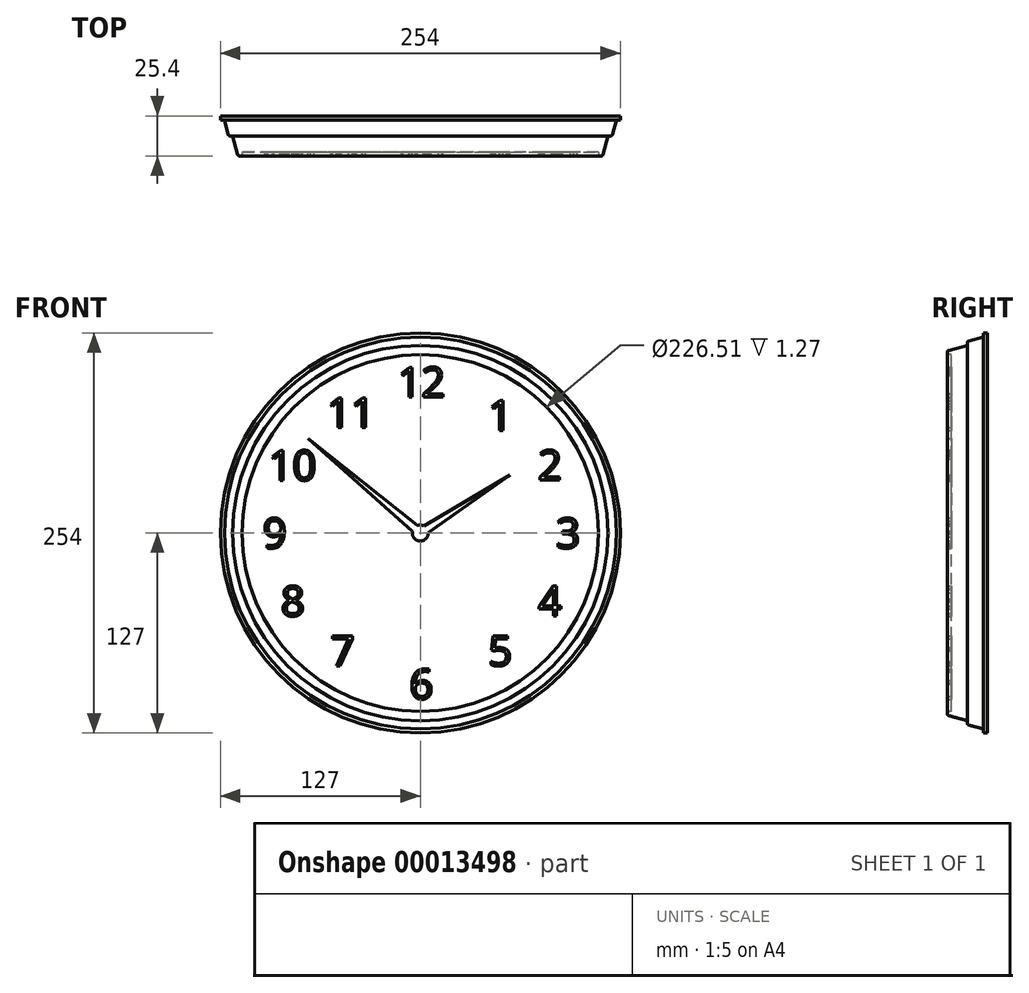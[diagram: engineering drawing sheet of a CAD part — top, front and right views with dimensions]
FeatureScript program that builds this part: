
annotation { "Feature Type Name" : "Feature", "Feature Type Description" : "" }
export const myFeature = defineFeature(function(context is Context, id is Id, definition is map)
    precondition{}
    {
        {
            var Q0;
            Q0=qCreatedBy(makeId("Right.planeOp"),FACE);
            var sketch = newSketch(context, id + "F0", { "sketchPlane" : qUnion([Q0])});
            skLineSegment(sketch, "E0", {"start": v(0, 0) * mm, "end": v(0, 127) * mm});
            skLineSegment(sketch, "E1", {"start": v(0, 127) * mm, "end": v(-2.54, 127) * mm});
            skLineSegment(sketch, "E2", {"start": v(-2.54, 127) * mm, "end": v(-2.54, 124.46) * mm});
            skLineSegment(sketch, "E3", {"start": v(-2.54, 124.46) * mm, "end": v(-11.76, 121.99) * mm});
            skLineSegment(sketch, "E4", {"start": v(-12.7, 120.76) * mm, "end": v(-12.7, 119.2) * mm});
            skLineSegment(sketch, "E5", {"start": v(-12.7, 119.2) * mm, "end": v(-24.46, 116.05) * mm});
            skLineSegment(sketch, "E6", {"start": v(-25.4, 114.82) * mm, "end": v(-25.4, 114.52) * mm});
            skLineSegment(sketch, "E7", {"start": v(-24.13, 113.25) * mm, "end": v(-22.86, 113.25) * mm});
            skLineSegment(sketch, "E8", {"start": v(-22.86, 113.25) * mm, "end": v(-22.86, 0) * mm});
            skLineSegment(sketch, "E9", {"start": v(-22.86, 0) * mm, "end": v(0, 0) * mm});
            skPoint(sketch, "E10.visualSharp", {"position": v(-12.7, 121.74) * mm});
            skArc(sketch, "E10.filletArc", {"start": v(-11.76, 121.99) * mm, "mid": v(-12.44, 121.54) * mm, "end": v(-12.7, 120.76) * mm});
            skPoint(sketch, "E11.visualSharp", {"position": v(-25.4, 115.8) * mm});
            skArc(sketch, "E11.filletArc", {"start": v(-24.46, 116.05) * mm, "mid": v(-25.14, 115.6) * mm, "end": v(-25.4, 114.82) * mm});
            skPoint(sketch, "E12.visualSharp", {"position": v(-25.4, 113.25) * mm});
            skArc(sketch, "E12.filletArc", {"start": v(-25.4, 114.52) * mm, "mid": v(-25.03, 113.63) * mm, "end": v(-24.13, 113.25) * mm});
            skSolve(sketch);
        }
        {
            var Q0;
            Q0 = qSketchRegion(id + "F0", true);
            var Q1;
            Q1=sQuery(id+"F0.wireOp",EDGE,"E9");
            revolve(context, id + "F1", {"entities" : qUnion([Q0]), "axis" : qUnion([Q1]), "revolveType" : RevolveType.FULL});
        }
        {
            var Q0;
            Q0=makeQuery(id+"F1.opRevolve","SWEPT_FACE",FACE,{"disambiguationData":[OSD([sQuery(id+"F0.wireOp",EDGE,"E8")])]});
            var sketch = newSketch(context, id + "F2", { "sketchPlane" : qUnion([Q0])});
            skText(sketch, "E13", { "text": "12", "fontName": "OpenSans-Regular.ttf"});
            skLineSegment(sketch, "E14", {"start": v(43.18, 74.79) * mm, "end": v(0, 0) * mm, "construction": true});
            skLineSegment(sketch, "E15", {"start": v(0, 0) * mm, "end": v(74.79, 43.18) * mm, "construction": true});
            skLineSegment(sketch, "E16", {"start": v(0, 0) * mm, "end": v(86.36, 0) * mm, "construction": true});
            skLineSegment(sketch, "E17", {"start": v(74.79, -43.18) * mm, "end": v(0, 0) * mm, "construction": true});
            skLineSegment(sketch, "E18", {"start": v(0, 0) * mm, "end": v(43.18, -74.79) * mm, "construction": true});
            skLineSegment(sketch, "E19", {"start": v(0, 0) * mm, "end": v(0, 86.36) * mm, "construction": true});
            skText(sketch, "E20", { "text": "1", "fontName": "OpenSans-Regular.ttf"});
            skText(sketch, "E21", { "text": "2", "fontName": "OpenSans-Regular.ttf"});
            skText(sketch, "E22", { "text": "3", "fontName": "OpenSans-Regular.ttf"});
            skLineSegment(sketch, "E23", {"start": v(0, 0) * mm, "end": v(0, -86.36) * mm, "construction": true});
            skText(sketch, "E24", { "text": "4", "fontName": "OpenSans-Regular.ttf"});
            skText(sketch, "E25", { "text": "5", "fontName": "OpenSans-Regular.ttf"});
            skText(sketch, "E26", { "text": "6", "fontName": "OpenSans-Regular.ttf"});
            skLineSegment(sketch, "E27", {"start": v(0, 0) * mm, "end": v(-43.18, -74.79) * mm, "construction": true});
            skLineSegment(sketch, "E28", {"start": v(0, 0) * mm, "end": v(-74.79, -43.18) * mm, "construction": true});
            skLineSegment(sketch, "E29", {"start": v(0, 0) * mm, "end": v(-74.79, 43.18) * mm, "construction": true});
            skLineSegment(sketch, "E30", {"start": v(0, 0) * mm, "end": v(-43.18, 74.79) * mm, "construction": true});
            skLineSegment(sketch, "E31", {"start": v(0, 0) * mm, "end": v(-86.36, 0) * mm, "construction": true});
            skText(sketch, "E32", { "text": "7", "fontName": "OpenSans-Regular.ttf"});
            skText(sketch, "E33", { "text": "8", "fontName": "OpenSans-Regular.ttf"});
            skText(sketch, "E34", { "text": "9", "fontName": "OpenSans-Regular.ttf"});
            skText(sketch, "E35", { "text": "10", "fontName": "OpenSans-Regular.ttf"});
            skText(sketch, "E36", { "text": "11", "fontName": "OpenSans-Regular.ttf"});
            const initialGuessF2  = {"E13": [-0.01442, 0.08636, 1, 0, 0.01905], "E20": [0.04318, 0.06526, 1, 0, 0.01905], "E21": [0.07479, 0.03366, 1, 0, 0.01905], "E22": [0.08636, -0.00953, 1, 0, 0.01905], "E24": [0.07479, -0.0527, 1, 0, 0.01905], "E25": [0.04318, -0.08431, 1, 0, 0.01905], "E26": [-0.00692, -0.10541, 1, 0, 0.01905], "E32": [-0.05696, -0.08431, 1, 0, 0.01905], "E33": [-0.08855, -0.0527, 1, 0, 0.01905], "E34": [-0.10007, -0.00953, 1, 0, 0.01905], "E35": [-0.09633, 0.03346, 1, 0, 0.01905], "E36": [-0.05927, 0.06695, 1, 0, 0.01905]};
            skSetInitialGuess(sketch, initialGuessF2);
            skSolve(sketch);
        }
        {
            var Q0;
            Q0 = qSketchRegion(id + "F2", true);
            extrude(context, id + "F3", {"entities" : qUnion([Q0]), "operationType" : NewBodyOperationType.ADD, "depth" : 2.54 * mm});
        }
        {
            var Q0;
            Q0=makeQuery(id+"F3.boolean.opBoolean","SPLIT",FACE,{"disambiguationData":[TD([makeQuery(id+"F1.opRevolve","SWEPT_FACE",FACE,{"disambiguationData":[OSD([sQuery(id+"F0.wireOp",EDGE,"E7")])]})])],"derivedFrom":makeQuery(id+"F1.opRevolve","SWEPT_FACE",FACE,{"disambiguationData":[OSD([sQuery(id+"F0.wireOp",EDGE,"E8")])]})});
            var sketch = newSketch(context, id + "F4", { "sketchPlane" : qUnion([Q0])});
            skLineSegment(sketch, "E37", {"start": v(56.84, 36.84) * mm, "end": v(5.06, 0.45) * mm});
            skLineSegment(sketch, "E38", {"start": v(2.48, 4.43) * mm, "end": v(56.84, 36.84) * mm});
            skLineSegment(sketch, "E39", {"start": v(-4.97, 1.03) * mm, "end": v(-71.17, 60.07) * mm});
            skLineSegment(sketch, "E40", {"start": v(-71.17, 60.07) * mm, "end": v(-1.85, 4.73) * mm});
            skArc(sketch, "E41", {"start": v(-4.97, 1.03) * mm, "mid": v(-0.3, -5.07) * mm, "end": v(5.06, 0.45) * mm});
            skArc(sketch, "E42.trimOffspring", {"start": v(2.48, 4.43) * mm, "mid": v(0.35, 5.07) * mm, "end": v(-1.85, 4.73) * mm});
            skSolve(sketch);
        }
        {
            var Q0;
            Q0 = qSketchRegion(id + "F4", true);
            extrude(context, id + "F5", {"entities" : qUnion([Q0]), "operationType" : NewBodyOperationType.ADD, "depth" : 2.54 * mm});
        }
    });
